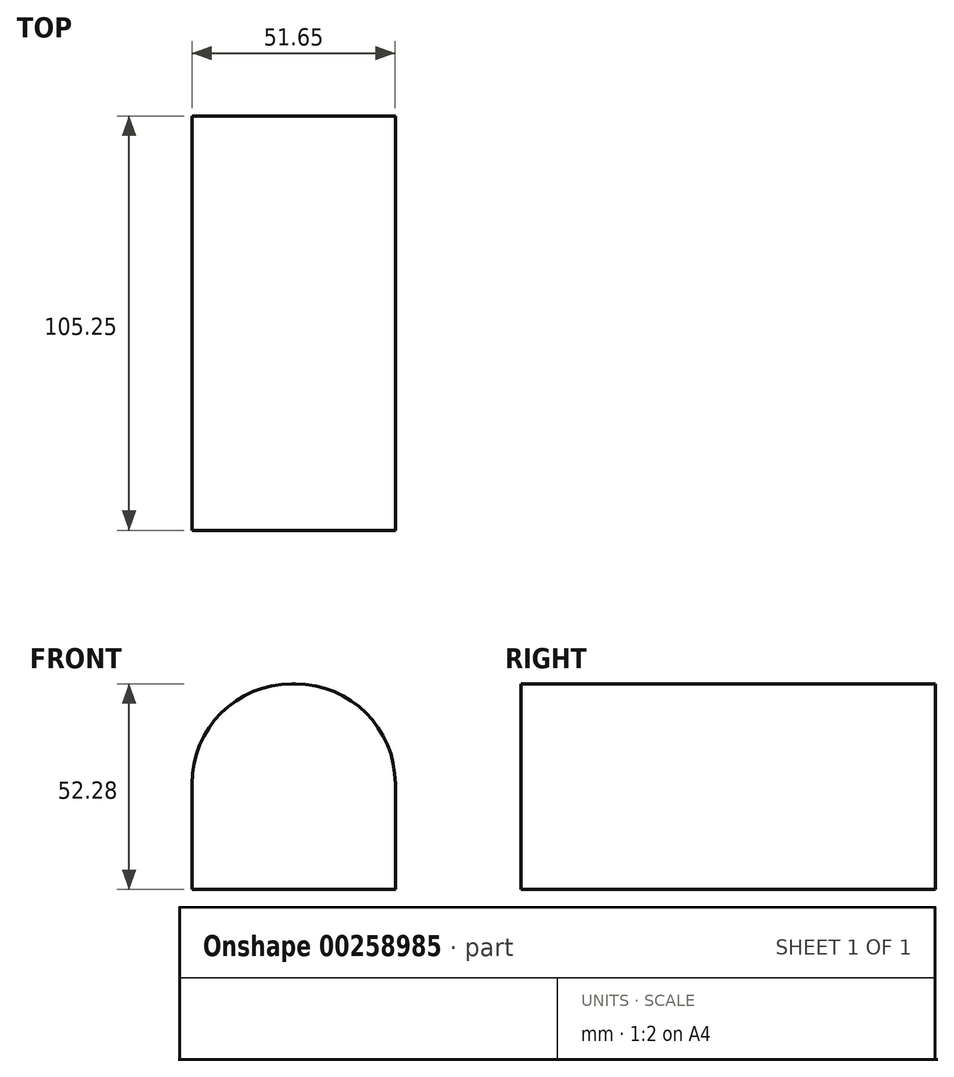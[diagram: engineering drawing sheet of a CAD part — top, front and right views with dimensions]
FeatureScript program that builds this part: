
annotation { "Feature Type Name" : "Feature", "Feature Type Description" : "" }
export const myFeature = defineFeature(function(context is Context, id is Id, definition is map)
    precondition{}
    {
        {
            var Q0;
            Q0=qCreatedBy(makeId("Front.planeOp"),FACE);
            var sketch = newSketch(context, id + "F0", { "sketchPlane" : qUnion([Q0])});
            skLineSegment(sketch, "E0.bottom", {"start": v(25.72, 35.9) * mm, "end": v(-25.93, 35.9) * mm});
            skLineSegment(sketch, "E0.top", {"start": v(25.72, -16.39) * mm, "end": v(-25.93, -16.39) * mm});
            skLineSegment(sketch, "E0.left", {"start": v(25.72, 35.9) * mm, "end": v(25.72, -16.39) * mm});
            skLineSegment(sketch, "E0.right", {"start": v(-25.93, 35.9) * mm, "end": v(-25.93, -16.39) * mm});
            skSolve(sketch);
        }
        {
            var Q0;
            Q0=makeQuery(id+"F0.imprint","IMPRINT",FACE,{"disambiguationData":[TD([[makeQuery(id+"F0.imprint","IMPRINT",EDGE,{"derivedFrom":sQuery(id+"F0.wireOp",EDGE,"E0.bottom")}),1.0]])]});
            extrude(context, id + "F1", {"entities" : qUnion([Q0]), "depth" : 105.25 * mm});
        }
        {
            var Q0;
            Q0=makeQuery(id+"F1.opExtrude","SWEPT_EDGE",EDGE,{"disambiguationData":[OSD([sQuery(id+"F0.wireOp",EDGE,"E0.bottom"),sQuery(id+"F0.wireOp",EDGE,"E0.right")])]});
            fillet(context, id + "F2", {"entities" : qUnion([Q0]), "radius" : 25.4 * mm, "tangentPropagation" : true, "allowEdgeOverflow" : false});
        }
        {
            var Q0;
            Q0=makeQuery(id+"F1.opExtrude","SWEPT_EDGE",EDGE,{"disambiguationData":[OSD([sQuery(id+"F0.wireOp",EDGE,"E0.bottom"),sQuery(id+"F0.wireOp",EDGE,"E0.left")])]});
            fillet(context, id + "F3", {"entities" : qUnion([Q0]), "radius" : 25.4 * mm, "tangentPropagation" : true, "allowEdgeOverflow" : false});
        }
    });
